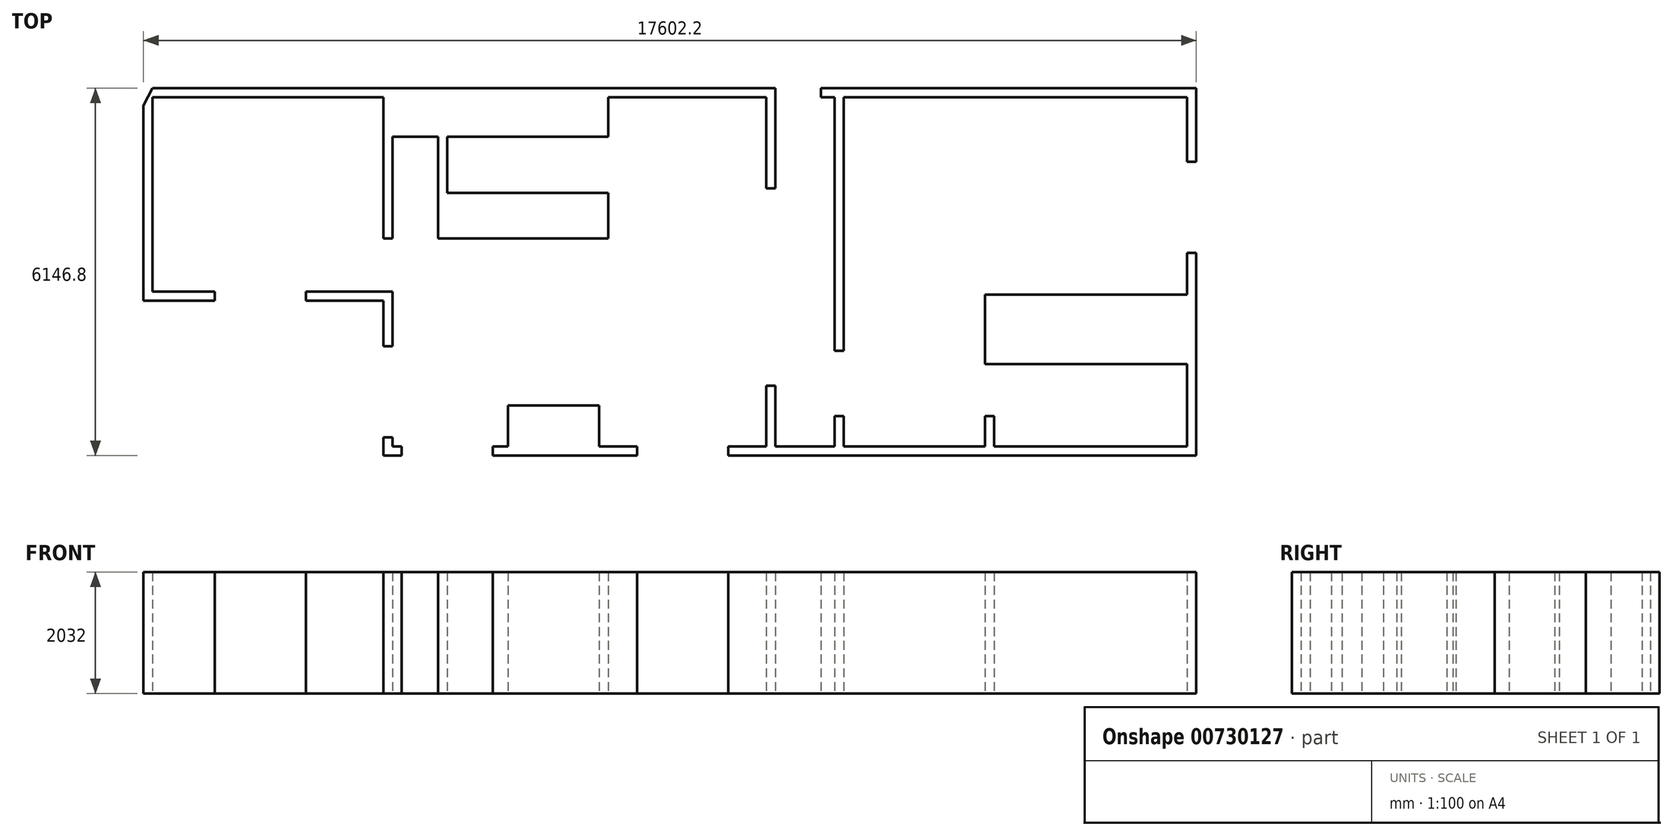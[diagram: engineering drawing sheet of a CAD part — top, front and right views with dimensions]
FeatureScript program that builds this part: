
annotation { "Feature Type Name" : "Feature", "Feature Type Description" : "" }
export const myFeature = defineFeature(function(context is Context, id is Id, definition is map)
    precondition{}
    {
        {
            var Q0;
            Q0=qCreatedBy(makeId("Top.planeOp"),FACE);
            var sketch = newSketch(context, id + "F0", { "sketchPlane" : qUnion([Q0])});
            skLineSegment(sketch, "E0.bottom", {"start": v(2652.57, 1758.5) * mm, "end": v(-3087.83, 1758.5) * mm});
            skLineSegment(sketch, "E0.top", {"start": v(2652.57, -1543.5) * mm, "end": v(-725.63, -1543.5) * mm});
            skLineSegment(sketch, "E0.left", {"start": v(2652.57, 1758.5) * mm, "end": v(2652.57, -1543.5) * mm});
            skLineSegment(sketch, "E0.right", {"start": v(-3087.83, 1758.5) * mm, "end": v(-3087.83, -1543.5) * mm});
            skLineSegment(sketch, "E1.top", {"start": v(-3087.83, -4083.5) * mm, "end": v(-725.63, -4083.5) * mm});
            skLineSegment(sketch, "E1.left", {"start": v(-3087.83, -1543.5) * mm, "end": v(-3087.83, -2483.3) * mm});
            skLineSegment(sketch, "E1.right", {"start": v(-725.63, -1543.5) * mm, "end": v(-725.63, -2706.62) * mm});
            skLineSegment(sketch, "E2.bottom", {"start": v(-725.63, -4083.5) * mm, "end": v(2652.57, -4083.5) * mm});
            skLineSegment(sketch, "E2.top", {"start": v(-725.63, -2706.62) * mm, "end": v(2652.57, -2706.62) * mm});
            skLineSegment(sketch, "E2.left", {"start": v(-725.63, -4083.5) * mm, "end": v(-725.63, -3575.5) * mm});
            skLineSegment(sketch, "E2.right", {"start": v(2652.57, -4083.5) * mm, "end": v(2652.57, -2706.62) * mm});
            skLineSegment(sketch, "E3.bottom", {"start": v(-725.63, -1543.5) * mm, "end": v(2652.57, -1543.5) * mm});
            skLineSegment(sketch, "E3.right", {"start": v(2652.57, -1543.5) * mm, "end": v(2652.57, -2706.62) * mm});
            skLineSegment(sketch, "E4.bottom", {"start": v(-3087.83, 1758.5) * mm, "end": v(-4230.83, 1758.5) * mm});
            skLineSegment(sketch, "E4.top", {"start": v(-3087.83, -4083.5) * mm, "end": v(-5017.5, -4083.5) * mm});
            skLineSegment(sketch, "E4.left", {"start": v(-3087.83, 1758.5) * mm, "end": v(-3087.83, -2483.3) * mm});
            skLineSegment(sketch, "E4.right", {"start": v(-4230.83, 1758.5) * mm, "end": v(-4230.83, 234.5) * mm});
            skLineSegment(sketch, "E5.bottom", {"start": v(-4383.23, 1758.5) * mm, "end": v(-4230.83, 1758.5) * mm});
            skLineSegment(sketch, "E5.top", {"start": v(-4383.23, 234.5) * mm, "end": v(-4230.83, 234.5) * mm});
            skLineSegment(sketch, "E5.right", {"start": v(-4383.23, 1758.5) * mm, "end": v(-4383.23, 234.5) * mm});
            skLineSegment(sketch, "E6.bottom", {"start": v(-3087.83, 1758.5) * mm, "end": v(-3240.23, 1758.5) * mm});
            skLineSegment(sketch, "E6.top", {"start": v(-3087.83, -2483.3) * mm, "end": v(-3240.23, -2483.3) * mm});
            skLineSegment(sketch, "E6.right", {"start": v(-3240.23, 1758.5) * mm, "end": v(-3240.23, -2483.3) * mm});
            skLineSegment(sketch, "E7.bottom", {"start": v(-3087.83, -4083.5) * mm, "end": v(-3240.23, -4083.5) * mm});
            skLineSegment(sketch, "E7.top", {"start": v(-3087.83, -3575.5) * mm, "end": v(-3240.23, -3575.5) * mm});
            skLineSegment(sketch, "E7.left", {"start": v(-3087.83, -4083.5) * mm, "end": v(-3087.83, -3575.5) * mm});
            skLineSegment(sketch, "E7.right", {"start": v(-3240.23, -4083.5) * mm, "end": v(-3240.23, -3575.5) * mm});
            skLineSegment(sketch, "E8.bottom", {"start": v(-4230.83, 1758.5) * mm, "end": v(-7024.83, 1758.5) * mm});
            skLineSegment(sketch, "E8.right", {"start": v(-7024.83, 1758.5) * mm, "end": v(-7024.83, 1098.1) * mm});
            skLineSegment(sketch, "E9.bottom", {"start": v(-7024.83, 1758.5) * mm, "end": v(-9869.63, 1758.5) * mm});
            skLineSegment(sketch, "E9.top", {"start": v(-7024.83, 1098.1) * mm, "end": v(-9869.63, 1098.1) * mm});
            skLineSegment(sketch, "E9.right", {"start": v(-9869.63, 1758.5) * mm, "end": v(-9869.63, 1098.1) * mm});
            skLineSegment(sketch, "E10.bottom", {"start": v(-7024.83, -603.7) * mm, "end": v(-9869.63, -603.7) * mm});
            skLineSegment(sketch, "E10.top", {"start": v(-6541.5, -4083.5) * mm, "end": v(-8955.23, -4083.5) * mm});
            skLineSegment(sketch, "E11.bottom", {"start": v(-9869.63, 1758.5) * mm, "end": v(-10784.03, 1758.5) * mm});
            skLineSegment(sketch, "E11.top", {"start": v(-10631.63, -603.7) * mm, "end": v(-10784.03, -603.7) * mm});
            skLineSegment(sketch, "E11.left", {"start": v(-9869.63, 1758.5) * mm, "end": v(-9869.63, -603.7) * mm});
            skLineSegment(sketch, "E11.right", {"start": v(-10784.03, 1758.5) * mm, "end": v(-10784.03, -603.7) * mm});
            skLineSegment(sketch, "E12.bottom", {"start": v(-10784.03, 1758.5) * mm, "end": v(-14644.83, 1758.5) * mm});
            skLineSegment(sketch, "E12.top", {"start": v(-10631.63, -1492.7) * mm, "end": v(-12083.78, -1492.7) * mm});
            skLineSegment(sketch, "E12.right", {"start": v(-14644.83, 1758.5) * mm, "end": v(-14644.83, -1492.7) * mm});
            skLineSegment(sketch, "E13.top", {"start": v(-11272.82, -603.7) * mm, "end": v(-10631.63, -603.7) * mm});
            skLineSegment(sketch, "E14.left", {"start": v(-10631.63, -1645.1) * mm, "end": v(-10631.63, -2407.1) * mm});
            skLineSegment(sketch, "E15.top", {"start": v(-7024.83, 158.3) * mm, "end": v(-9869.63, 158.3) * mm});
            skLineSegment(sketch, "E15.left", {"start": v(-7024.83, -603.7) * mm, "end": v(-7024.83, 158.3) * mm});
            skLineSegment(sketch, "E15.right", {"start": v(-9869.63, -603.7) * mm, "end": v(-9869.63, 158.3) * mm});
            skLineSegment(sketch, "E16.trimOffspring", {"start": v(-7024.83, 158.3) * mm, "end": v(-7024.83, -603.7) * mm});
            skLineSegment(sketch, "E17.bottom", {"start": v(-9869.63, 1758.5) * mm, "end": v(-9717.23, 1758.5) * mm});
            skLineSegment(sketch, "E17.top", {"start": v(-9869.63, -603.7) * mm, "end": v(-9717.23, -603.7) * mm});
            skLineSegment(sketch, "E17.right", {"start": v(-9717.23, 1758.5) * mm, "end": v(-9717.23, -603.7) * mm});
            skLineSegment(sketch, "E18.bottom", {"start": v(-10784.03, 1758.5) * mm, "end": v(-10631.63, 1758.5) * mm});
            skLineSegment(sketch, "E18.top", {"start": v(-10784.03, -603.7) * mm, "end": v(-10631.63, -603.7) * mm});
            skLineSegment(sketch, "E18.right", {"start": v(-10631.63, 1098.1) * mm, "end": v(-10631.63, -603.7) * mm});
            skLineSegment(sketch, "E19.bottom", {"start": v(-10784.03, 1758.5) * mm, "end": v(-9869.63, 1758.5) * mm});
            skLineSegment(sketch, "E19.top", {"start": v(-10784.03, 1098.1) * mm, "end": v(-9869.63, 1098.1) * mm});
            skLineSegment(sketch, "E19.left", {"start": v(-10784.03, 1758.5) * mm, "end": v(-10784.03, 1098.1) * mm});
            skLineSegment(sketch, "E20.bottom", {"start": v(-8701.23, -4083.5) * mm, "end": v(-7177.23, -4083.5) * mm});
            skLineSegment(sketch, "E20.top", {"start": v(-8701.23, -3397.7) * mm, "end": v(-7177.23, -3397.7) * mm});
            skLineSegment(sketch, "E20.left", {"start": v(-8701.23, -4083.5) * mm, "end": v(-8701.23, -3397.7) * mm});
            skLineSegment(sketch, "E20.right", {"start": v(-7177.23, -4083.5) * mm, "end": v(-7177.23, -3397.7) * mm});
            skLineSegment(sketch, "E21.top", {"start": v(-10784.03, -1645.1) * mm, "end": v(-12083.78, -1645.1) * mm});
            skLineSegment(sketch, "E22.bottom", {"start": v(-10631.63, -4083.5) * mm, "end": v(-10784.03, -4083.5) * mm});
            skLineSegment(sketch, "E22.top", {"start": v(-10631.63, -3931.1) * mm, "end": v(-10784.03, -3931.1) * mm});
            skLineSegment(sketch, "E22.left", {"start": v(-10631.63, -4083.5) * mm, "end": v(-10631.63, -3931.1) * mm});
            skLineSegment(sketch, "E22.right", {"start": v(-10784.03, -4083.5) * mm, "end": v(-10784.03, -3931.1) * mm});
            skLineSegment(sketch, "E23.top", {"start": v(-10631.63, -2407.1) * mm, "end": v(-10784.03, -2407.1) * mm});
            skLineSegment(sketch, "E23.left", {"start": v(-10631.63, -1492.7) * mm, "end": v(-10631.63, -2407.1) * mm});
            skLineSegment(sketch, "E23.right", {"start": v(-10784.03, -1645.1) * mm, "end": v(-10784.03, -2407.1) * mm});
            skLineSegment(sketch, "E24.bottom", {"start": v(-10784.03, -4083.5) * mm, "end": v(-10479.23, -4083.5) * mm});
            skLineSegment(sketch, "E24.top", {"start": v(-10784.03, -4235.9) * mm, "end": v(-10479.23, -4235.9) * mm});
            skLineSegment(sketch, "E24.left", {"start": v(-10784.03, -4083.5) * mm, "end": v(-10784.03, -4235.9) * mm});
            skLineSegment(sketch, "E24.right", {"start": v(-10479.23, -4083.5) * mm, "end": v(-10479.23, -4235.9) * mm});
            skLineSegment(sketch, "E25.bottom", {"start": v(-8955.23, -4083.5) * mm, "end": v(-6541.5, -4083.5) * mm});
            skLineSegment(sketch, "E25.top", {"start": v(-8955.23, -4235.9) * mm, "end": v(-6541.5, -4235.9) * mm});
            skLineSegment(sketch, "E25.left", {"start": v(-8955.23, -4083.5) * mm, "end": v(-8955.23, -4235.9) * mm});
            skLineSegment(sketch, "E25.right", {"start": v(-6541.5, -4083.5) * mm, "end": v(-6541.5, -4235.9) * mm});
            skLineSegment(sketch, "E26.bottom", {"start": v(-5017.5, -4083.5) * mm, "end": v(2652.57, -4083.5) * mm});
            skLineSegment(sketch, "E26.top", {"start": v(-5017.5, -4235.9) * mm, "end": v(2804.97, -4235.9) * mm});
            skLineSegment(sketch, "E26.left", {"start": v(-5017.5, -4083.5) * mm, "end": v(-5017.5, -4235.9) * mm});
            skLineSegment(sketch, "E27.bottom", {"start": v(2652.57, -844.43) * mm, "end": v(2804.97, -844.43) * mm});
            skLineSegment(sketch, "E27.left", {"start": v(2652.57, -844.43) * mm, "end": v(2652.57, -4083.5) * mm});
            skLineSegment(sketch, "E27.right", {"start": v(2804.97, -844.43) * mm, "end": v(2804.97, -4235.9) * mm});
            skLineSegment(sketch, "E28.bottom", {"start": v(2652.57, 1758.5) * mm, "end": v(2804.97, 1758.5) * mm});
            skLineSegment(sketch, "E28.top", {"start": v(2652.57, 679.57) * mm, "end": v(2804.97, 679.57) * mm});
            skLineSegment(sketch, "E28.left", {"start": v(2652.57, 1758.5) * mm, "end": v(2652.57, 679.57) * mm});
            skLineSegment(sketch, "E28.right", {"start": v(2804.97, 1758.5) * mm, "end": v(2804.97, 679.57) * mm});
            skLineSegment(sketch, "E29.bottom", {"start": v(2804.97, 1758.5) * mm, "end": v(-3468.83, 1758.5) * mm});
            skLineSegment(sketch, "E29.top", {"start": v(2804.97, 1910.9) * mm, "end": v(-3468.83, 1910.9) * mm});
            skLineSegment(sketch, "E29.left", {"start": v(2804.97, 1758.5) * mm, "end": v(2804.97, 1910.9) * mm});
            skLineSegment(sketch, "E29.right", {"start": v(-3468.83, 1758.5) * mm, "end": v(-3468.83, 1910.9) * mm});
            skLineSegment(sketch, "E30.bottom", {"start": v(-14644.83, 1758.5) * mm, "end": v(-4230.83, 1758.5) * mm});
            skLineSegment(sketch, "E30.top", {"start": v(-14644.83, 1910.9) * mm, "end": v(-4230.83, 1910.9) * mm});
            skLineSegment(sketch, "E30.left", {"start": v(-14644.83, 1758.5) * mm, "end": v(-14644.83, 1910.9) * mm});
            skLineSegment(sketch, "E30.right", {"start": v(-4230.83, 1758.5) * mm, "end": v(-4230.83, 1910.9) * mm});
            skLineSegment(sketch, "E31.bottom", {"start": v(-14644.83, 1910.9) * mm, "end": v(-14797.23, 1620.34) * mm});
            skLineSegment(sketch, "E31.left", {"start": v(-14644.83, 1910.9) * mm, "end": v(-14644.83, -1492.7) * mm});
            skLineSegment(sketch, "E31.right", {"start": v(-14797.23, 1620.34) * mm, "end": v(-14797.23, -1645.1) * mm});
            skLineSegment(sketch, "E32.trimOffspring", {"start": v(-3087.83, -3575.5) * mm, "end": v(-3087.83, -4083.5) * mm});
            skLineSegment(sketch, "E33.trimOffspring", {"start": v(-10479.23, -4083.5) * mm, "end": v(-10631.63, -4083.5) * mm});
            skLineSegment(sketch, "E34.trimOffspring", {"start": v(-10631.63, -3931.1) * mm, "end": v(-10631.63, -4083.5) * mm});
            skLineSegment(sketch, "E35.bottom", {"start": v(-725.63, -4083.5) * mm, "end": v(-573.23, -4083.5) * mm});
            skLineSegment(sketch, "E35.top", {"start": v(-725.63, -3575.5) * mm, "end": v(-573.23, -3575.5) * mm});
            skLineSegment(sketch, "E35.right", {"start": v(-573.23, -4083.5) * mm, "end": v(-573.23, -3575.5) * mm});
            skLineSegment(sketch, "E36.trimOffspring", {"start": v(-725.63, -3575.5) * mm, "end": v(-725.63, -4083.5) * mm});
            skLineSegment(sketch, "E37.bottom", {"start": v(-4383.23, -4083.5) * mm, "end": v(-4230.83, -4083.5) * mm});
            skLineSegment(sketch, "E37.top", {"start": v(-4383.23, -3067.5) * mm, "end": v(-4230.83, -3067.5) * mm});
            skLineSegment(sketch, "E37.left", {"start": v(-4230.83, -4083.5) * mm, "end": v(-4230.83, -3067.5) * mm});
            skLineSegment(sketch, "E37.right", {"start": v(-4383.23, -4083.5) * mm, "end": v(-4383.23, -3067.5) * mm});
            skPoint(sketch, "E26.right.end.orphan", {"position": v(2125.52, -4235.9) * mm});
            skLineSegment(sketch, "E38.left", {"start": v(-13607.78, -1751.26) * mm, "end": v(-13607.78, -1492.7) * mm});
            skLineSegment(sketch, "E38.right", {"start": v(-12083.78, -1751.26) * mm, "end": v(-12083.78, -1492.7) * mm});
            skLineSegment(sketch, "E39.trimOffspring", {"start": v(-13607.78, -1492.7) * mm, "end": v(-14644.83, -1492.7) * mm});
            skLineSegment(sketch, "E40.trimOffspring", {"start": v(-13607.78, -1645.1) * mm, "end": v(-14797.23, -1645.1) * mm});
            skSolve(sketch);
        }
        {
            var Q0;
            {var subQ0=sQuery(id+"F0.wireOp",EDGE,"E10.bottom");Q0=makeQuery(id+"F0.imprint","IMPRINT",FACE,{"disambiguationData":[TD([[makeQuery(id+"F0.imprint","IMPRINT",EDGE,{"derivedFrom":subQ0}),-1.0]])]});}
            var sketch = newSketch(context, id + "F1", { "sketchPlane" : qUnion([Q0])});
            skLineSegment(sketch, "E41.bottom", {"start": v(-5933.83, -156.72) * mm, "end": v(-5032.13, -156.72) * mm});
            skLineSegment(sketch, "E41.top", {"start": v(-5933.83, -1985.52) * mm, "end": v(-5032.13, -1985.52) * mm});
            skLineSegment(sketch, "E41.left", {"start": v(-5933.83, -156.72) * mm, "end": v(-5933.83, -1985.52) * mm});
            skLineSegment(sketch, "E41.right", {"start": v(-5032.13, -156.72) * mm, "end": v(-5032.13, -1985.52) * mm});
            skSolve(sketch);
        }
        {
            var Q0;
            Q0 = qSketchRegion(id + "F0", true);
            extrude(context, id + "F2", {"entities" : qUnion([Q0]), "depth" : 2032 * mm, "offsetDistance" : 25.4 * mm});
        }
    });
